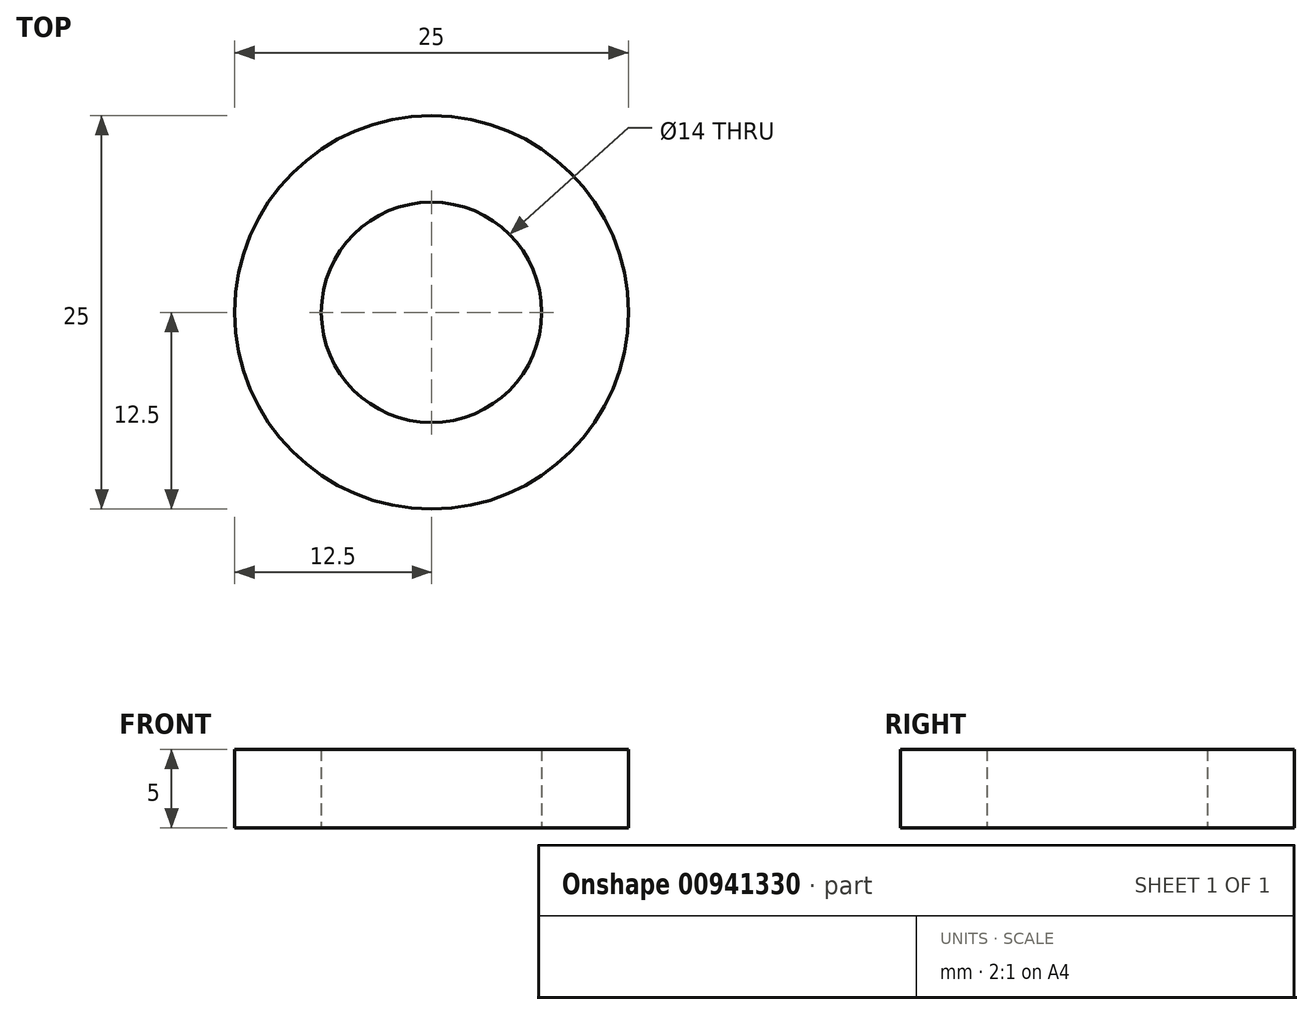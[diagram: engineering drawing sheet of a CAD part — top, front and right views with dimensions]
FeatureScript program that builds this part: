
annotation { "Feature Type Name" : "Feature", "Feature Type Description" : "" }
export const myFeature = defineFeature(function(context is Context, id is Id, definition is map)
    precondition{}
    {
        {
            var Q0;
            Q0=qCreatedBy(makeId("Top.planeOp"),FACE);
            var sketch = newSketch(context, id + "F0", { "sketchPlane" : qUnion([Q0])});
            skCircle(sketch, "E0", {"center": v(0, 0) * mm, "radius": 7 * mm});
            skCircle(sketch, "E1", {"center": v(0, 0) * mm, "radius": 12.5 * mm});
            skSolve(sketch);
        }
        {
            var Q0;
            Q0=makeQuery(id+"F0.imprint","IMPRINT",FACE,{"disambiguationData":[TD([[makeQuery(id+"F0.imprint","IMPRINT",EDGE,{"derivedFrom":sQuery(id+"F0.wireOp",EDGE,"E0")}),-1.0]])]});
            extrude(context, id + "F1", {"entities" : qUnion([Q0]), "depth" : 5 * mm, "offsetDistance" : 25 * mm});
        }
    });
